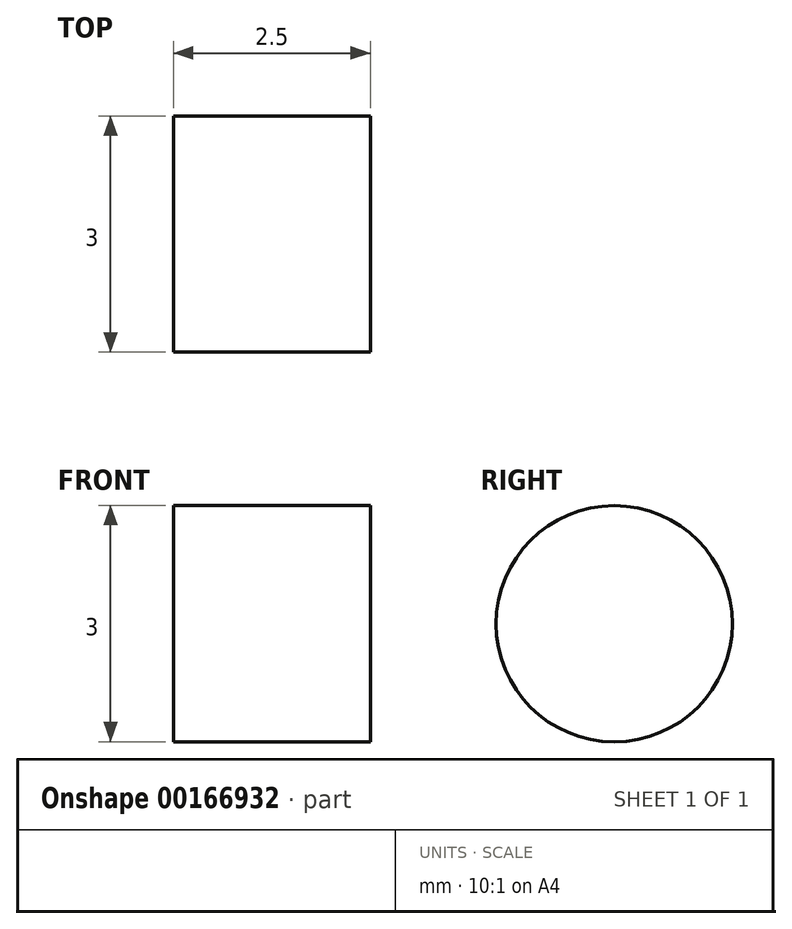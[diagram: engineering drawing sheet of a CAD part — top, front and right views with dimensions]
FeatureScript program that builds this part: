
annotation { "Feature Type Name" : "Feature", "Feature Type Description" : "" }
export const myFeature = defineFeature(function(context is Context, id is Id, definition is map)
    precondition{}
    {
        {
            var Q0;
            Q0=qCreatedBy(makeId("Right.planeOp"),FACE);
            var sketch = newSketch(context, id + "F0", { "sketchPlane" : qUnion([Q0])});
            skCircle(sketch, "E0", {"center": v(-39.76, 32.83) * mm, "radius": 1.5 * mm});
            skCircle(sketch, "E1", {"center": v(-39.76, -59.17) * mm, "radius": 1.5 * mm});
            skCircle(sketch, "E2", {"center": v(39.24, 66.83) * mm, "radius": 1.5 * mm});
            skCircle(sketch, "E3", {"center": v(-0.76, -64.17) * mm, "radius": 1.5 * mm});
            skCircle(sketch, "E4", {"center": v(4.74, 0.83) * mm, "radius": 6 * mm});
            skLineSegment(sketch, "E5", {"start": v(-14.19, -8.89) * mm, "end": v(5.8, 22.76) * mm});
            skArc(sketch, "E6", {"start": v(5.8, 22.76) * mm, "mid": v(5.86, 24.8) * mm, "end": v(4.1, 25.83) * mm});
            skLineSegment(sketch, "E7", {"start": v(4.1, 25.83) * mm, "end": v(-28.79, 25.83) * mm});
            skArc(sketch, "E8", {"start": v(-28.79, 25.83) * mm, "mid": v(-30.45, 24.94) * mm, "end": v(-30.64, 23.07) * mm});
            skLineSegment(sketch, "E9", {"start": v(-30.64, 23.07) * mm, "end": v(-17.73, -8.57) * mm});
            skArc(sketch, "E10", {"start": v(-17.73, -8.57) * mm, "mid": v(-16.05, -9.81) * mm, "end": v(-14.19, -8.89) * mm});
            skArc(sketch, "E11", {"start": v(-10.79, -59.53) * mm, "mid": v(-9.34, -58.55) * mm, "end": v(-9.2, -56.8) * mm});
            skLineSegment(sketch, "E12", {"start": v(-9.2, -56.8) * mm, "end": v(-16.81, -37.8) * mm});
            skArc(sketch, "E13", {"start": v(-16.81, -37.8) * mm, "mid": v(-18.48, -36.54) * mm, "end": v(-20.36, -37.46) * mm});
            skLineSegment(sketch, "E14", {"start": v(-20.36, -37.46) * mm, "end": v(-34.43, -59.51) * mm});
            skArc(sketch, "E15", {"start": v(-34.43, -59.51) * mm, "mid": v(-34.42, -61.67) * mm, "end": v(-32.46, -62.57) * mm});
            skLineSegment(sketch, "E16", {"start": v(-32.46, -62.57) * mm, "end": v(-10.79, -59.53) * mm});
            skLineSegment(sketch, "E17", {"start": v(-29.08, -32.97) * mm, "end": v(-23.32, -24.04) * mm});
            skArc(sketch, "E18", {"start": v(-23.32, -24.04) * mm, "mid": v(-23.01, -23.15) * mm, "end": v(-23.15, -22.21) * mm});
            skLineSegment(sketch, "E19", {"start": v(-23.15, -22.21) * mm, "end": v(-28.9, -7.81) * mm});
            skArc(sketch, "E20", {"start": v(-28.9, -7.81) * mm, "mid": v(-31.14, -6.6) * mm, "end": v(-32.76, -8.56) * mm});
            skLineSegment(sketch, "E21", {"start": v(-32.76, -8.56) * mm, "end": v(-32.76, -31.88) * mm});
            skArc(sketch, "E22", {"start": v(-32.76, -31.88) * mm, "mid": v(-31.33, -33.8) * mm, "end": v(-29.08, -32.97) * mm});
            skLineSegment(sketch, "E23", {"start": v(-11.26, -23.3) * mm, "end": v(-6.5, -15.1) * mm});
            skArc(sketch, "E24", {"start": v(-6.5, -15.1) * mm, "mid": v(-4.24, -14.17) * mm, "end": v(-2.76, -16.1) * mm});
            skLineSegment(sketch, "E25", {"start": v(-2.76, -16.1) * mm, "end": v(-2.76, -35.43) * mm});
            skArc(sketch, "E26", {"start": v(-2.76, -35.43) * mm, "mid": v(-4.36, -37.39) * mm, "end": v(-6.6, -36.22) * mm});
            skLineSegment(sketch, "E27", {"start": v(-6.6, -36.22) * mm, "end": v(-11.37, -25.1) * mm});
            skArc(sketch, "E28", {"start": v(-11.37, -25.1) * mm, "mid": v(-11.52, -24.19) * mm, "end": v(-11.26, -23.3) * mm});
            skLineSegment(sketch, "E29", {"start": v(-44.76, -56.67) * mm, "end": v(-44.76, -67.17) * mm});
            skArc(sketch, "E30", {"start": v(-44.76, -67.17) * mm, "mid": v(-43.3, -70.7) * mm, "end": v(-39.76, -72.17) * mm});
            skLineSegment(sketch, "E31", {"start": v(-39.76, -72.17) * mm, "end": v(-31.57, -72.17) * mm});
            skArc(sketch, "E32", {"start": v(-31.57, -72.17) * mm, "mid": v(-31.26, -72.16) * mm, "end": v(-30.95, -72.13) * mm});
            skLineSegment(sketch, "E33", {"start": v(-30.95, -72.13) * mm, "end": v(-7.57, -69.21) * mm});
            skArc(sketch, "E34", {"start": v(-7.57, -69.21) * mm, "mid": v(-7.26, -69.18) * mm, "end": v(-6.95, -69.17) * mm});
            skLineSegment(sketch, "E35", {"start": v(-6.95, -69.17) * mm, "end": v(-0.76, -69.17) * mm});
            skArc(sketch, "E36", {"start": v(-0.76, -69.17) * mm, "mid": v(2.77, -67.7) * mm, "end": v(4.24, -64.17) * mm});
            skLineSegment(sketch, "E37", {"start": v(4.24, -64.17) * mm, "end": v(4.24, -28.2) * mm});
            skArc(sketch, "E38", {"start": v(4.24, -28.2) * mm, "mid": v(4.34, -27.2) * mm, "end": v(4.64, -26.23) * mm});
            skLineSegment(sketch, "E39", {"start": v(4.64, -26.23) * mm, "end": v(44.35, 64.98) * mm});
            skArc(sketch, "E40", {"start": v(44.35, 64.98) * mm, "mid": v(44.46, 68.68) * mm, "end": v(42, 71.45) * mm});
            skLineSegment(sketch, "E41", {"start": v(42, 71.45) * mm, "end": v(41.6, 71.64) * mm});
            skArc(sketch, "E42", {"start": v(41.6, 71.64) * mm, "mid": v(37.84, 71.93) * mm, "end": v(34.95, 69.51) * mm});
            skLineSegment(sketch, "E43", {"start": v(34.95, 69.51) * mm, "end": v(23.12, 47.2) * mm});
            skArc(sketch, "E44", {"start": v(23.12, 47.2) * mm, "mid": v(18.7, 42.55) * mm, "end": v(12.52, 40.83) * mm});
            skLineSegment(sketch, "E45", {"start": v(12.52, 40.83) * mm, "end": v(-38.22, 40.83) * mm});
            skArc(sketch, "E46", {"start": v(-38.22, 40.83) * mm, "mid": v(-42.84, 38.71) * mm, "end": v(-44.26, 33.83) * mm});
            skArc(sketch, "E47", {"start": v(-44.26, 33.83) * mm, "mid": v(-41.06, -11.44) * mm, "end": v(-44.76, -56.67) * mm});
            skSolve(sketch);
        }
        {
            var Q0;
            Q0=makeQuery(id+"F0.imprint","IMPRINT",FACE,{"disambiguationData":[TD([[makeQuery(id+"F0.imprint","IMPRINT",EDGE,{"derivedFrom":sQuery(id+"F0.wireOp",EDGE,"E0")}),1.0]])]});
            extrude(context, id + "F1", {"entities" : qUnion([Q0]), "endBound" : BoundingType.SYMMETRIC, "depth" : 2.5 * mm});
        }
    });
